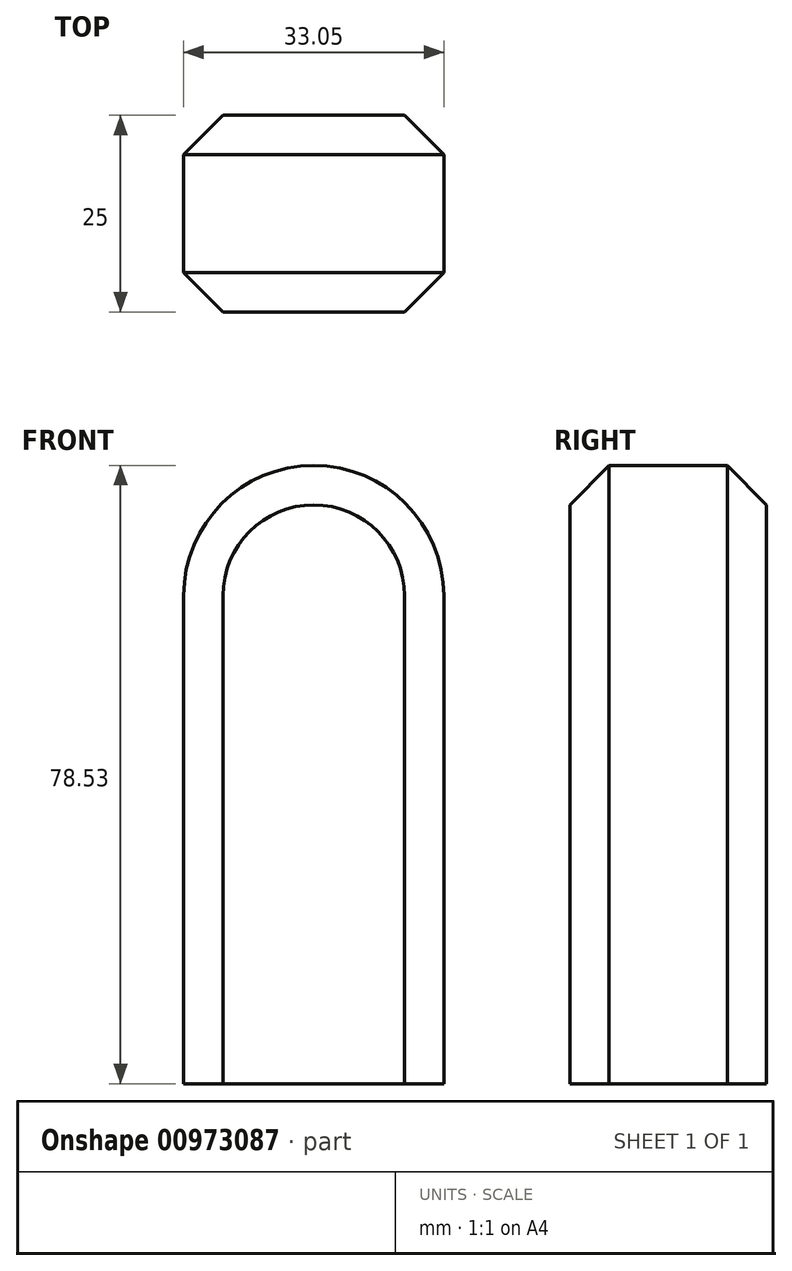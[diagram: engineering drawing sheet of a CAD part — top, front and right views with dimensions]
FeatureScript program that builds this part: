
annotation { "Feature Type Name" : "Feature", "Feature Type Description" : "" }
export const myFeature = defineFeature(function(context is Context, id is Id, definition is map)
    precondition{}
    {
        {
            var Q0;
            Q0=qCreatedBy(makeId("Front.planeOp"),FACE);
            var sketch = newSketch(context, id + "F0", { "sketchPlane" : qUnion([Q0])});
            skLineSegment(sketch, "E0.bottom", {"start": v(0, 0) * mm, "end": v(33.05, 0) * mm});
            skLineSegment(sketch, "E0.left", {"start": v(0, 0) * mm, "end": v(0, 62) * mm});
            skLineSegment(sketch, "E0.right", {"start": v(33.05, 0) * mm, "end": v(33.05, 62) * mm});
            skArc(sketch, "E1", {"start": v(33.05, 62) * mm, "mid": v(16.52, 78.53) * mm, "end": v(0, 62) * mm});
            skSolve(sketch);
        }
        {
            var Q0;
            Q0 = qSketchRegion(id + "F0", true);
            extrude(context, id + "F1", {"entities" : qUnion([Q0]), "endBound" : BoundingType.SYMMETRIC, "depth" : 25 * mm, "offsetDistance" : 25 * mm});
        }
        {
            var Q0;
            Q0=makeQuery(id+"F1.opExtrude","CAP_EDGE",EDGE,{"disambiguationData":[OSD([sQuery(id+"F0.wireOp",EDGE,"E1")])],"isStart":false});
            var Q1;
            Q1=makeQuery(id+"F1.opExtrude","CAP_EDGE",EDGE,{"disambiguationData":[OSD([sQuery(id+"F0.wireOp",EDGE,"E1")])],"isStart":true});
            chamfer(context, id + "F2", {"entities" : qUnion([Q0, Q1]), "width" : 5 * mm, "tangentPropagation" : true});
        }
    });
